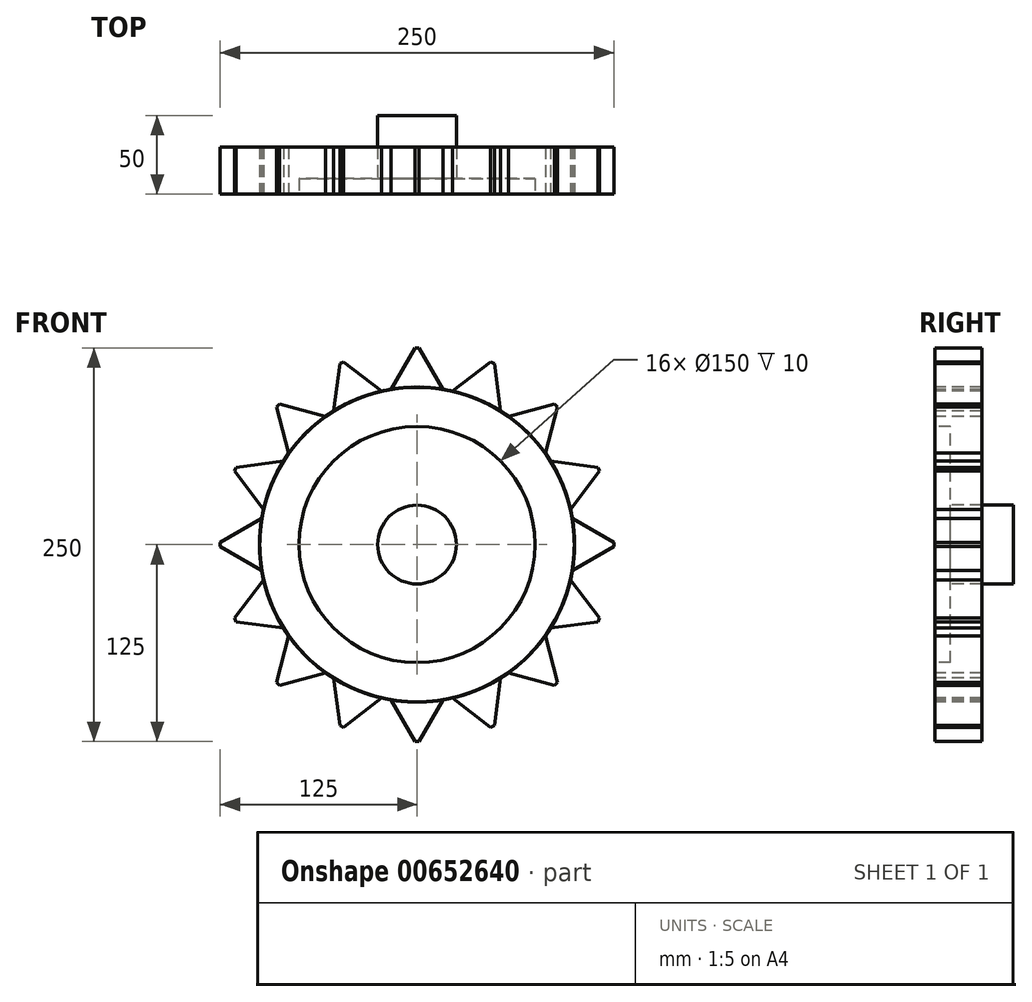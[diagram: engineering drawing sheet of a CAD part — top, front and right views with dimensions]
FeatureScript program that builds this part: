
annotation { "Feature Type Name" : "Feature", "Feature Type Description" : "" }
export const myFeature = defineFeature(function(context is Context, id is Id, definition is map)
    precondition{}
    {
        {
            var Q0;
            Q0=qCreatedBy(makeId("Front.planeOp"),FACE);
            var sketch = newSketch(context, id + "F0", { "sketchPlane" : qUnion([Q0])});
            skCircle(sketch, "E0", {"center": v(0, 0) * mm, "radius": 100 * mm});
            skSolve(sketch);
        }
        {
            var Q0;
            Q0=makeQuery(id+"F0.imprint","IMPRINT",FACE,{"disambiguationData":[TD([[makeQuery(id+"F0.imprint","IMPRINT",EDGE,{"derivedFrom":sQuery(id+"F0.wireOp",EDGE,"E0")}),1.0]])]});
            extrude(context, id + "F1", {"entities" : qUnion([Q0]), "oppositeDirection" : true, "depth" : 30 * mm, "offsetDistance" : 25 * mm});
        }
        {
            var Q0;
            Q0=makeQuery(id+"F1.opExtrude","CAP_FACE",FACE,{"disambiguationData":[OSD([sQuery(id+"F0.wireOp",EDGE,"E0")])],"isStart":true});
            var sketch = newSketch(context, id + "F2", { "sketchPlane" : qUnion([Q0])});
            skLineSegment(sketch, "E1", {"start": v(-23.1, 97.3) * mm, "end": v(-23.1, 87.3) * mm, "construction": true});
            skLineSegment(sketch, "E2", {"start": v(-23.1, 87.3) * mm, "end": v(23.1, 87.3) * mm, "construction": true});
            skLineSegment(sketch, "E3", {"start": v(23.1, 87.3) * mm, "end": v(23.1, 97.3) * mm, "construction": true});
            skLineSegment(sketch, "E4", {"start": v(23.1, 97.3) * mm, "end": v(23.1, 127.3) * mm, "construction": true});
            skLineSegment(sketch, "E5", {"start": v(23.1, 127.3) * mm, "end": v(-23.1, 127.3) * mm, "construction": true});
            skLineSegment(sketch, "E6", {"start": v(-23.1, 127.3) * mm, "end": v(-23.1, 97.3) * mm, "construction": true});
            skLineSegment(sketch, "E7", {"start": v(0, 127.3) * mm, "end": v(0, 87.3) * mm, "construction": true});
            skLineSegment(sketch, "E8", {"start": v(0, 127.3) * mm, "end": v(-23.1, 87.3) * mm, "construction": true});
            skLineSegment(sketch, "E9", {"start": v(23.1, 87.3) * mm, "end": v(0, 127.3) * mm, "construction": true});
            skLineSegment(sketch, "E10", {"start": v(0, 100) * mm, "end": v(0, 125) * mm, "construction": true});
            skLineSegment(sketch, "E11", {"start": v(0, 125) * mm, "end": v(1.33, 125) * mm, "construction": true});
            skLineSegment(sketch, "E12", {"start": v(1.33, 125) * mm, "end": v(0, 125) * mm, "construction": true});
            skLineSegment(sketch, "E13", {"start": v(0, 125) * mm, "end": v(-1.33, 125) * mm});
            skLineSegment(sketch, "E14", {"start": v(-1.33, 125) * mm, "end": v(-16.56, 98.62) * mm});
            skLineSegment(sketch, "E15", {"start": v(-16.56, 98.62) * mm, "end": v(-1.33, 125) * mm});
            skLineSegment(sketch, "E16", {"start": v(0, 125) * mm, "end": v(1.33, 125) * mm});
            skLineSegment(sketch, "E17", {"start": v(1.33, 125) * mm, "end": v(16.56, 98.62) * mm});
            skLineSegment(sketch, "E18", {"start": v(16.56, 98.62) * mm, "end": v(-16.56, 98.62) * mm});
            skSolve(sketch);
        }
        {
            var Q0;
            Q0=qSketchRegion(id+"F2",true);
            extrude(context, id + "F3", {"entities" : qUnion([Q0]), "operationType" : NewBodyOperationType.ADD, "oppositeDirection" : true, "depth" : 30 * mm, "offsetDistance" : 25 * mm});
        }
        {
            var Q0;
            Q0=qCreatedBy(makeId("Top.planeOp"),FACE);
            var sketch = newSketch(context, id + "F4", { "sketchPlane" : qUnion([Q0])});
            skLineSegment(sketch, "E19", {"start": v(0, 76.88) * mm, "end": v(0, -72) * mm, "construction": true});
            skSolve(sketch);
        }
        {
            var Q0;
            Q0=makeQuery(id+"F1.opExtrude","SWEPT_BODY",BODY,{"disambiguationData":[OSD([sQuery(id+"F0.wireOp",EDGE,"E0")])]});
            var Q1;
            Q1=sQuery(id+"F4.wireOp",EDGE,"E19");
            circularPattern(context, id + "F5", {"entities" : qUnion([Q0]), "axis" : qUnion([Q1]), "angle" : 360 * degree, "instanceCount" : 16, "equalSpace" : true});
        }
        {
            var Q0;
            Q0=makeQuery(id+"F3.boolean.opBoolean","MERGE",FACE,{"derivedFrom":[makeQuery(id+"F1.opExtrude","CAP_FACE",FACE,{"disambiguationData":[OSD([sQuery(id+"F0.wireOp",EDGE,"E0")])],"isStart":true}),makeQuery(id+"F3.opExtrude","CAP_FACE",FACE,{"disambiguationData":[OSD([sQuery(id+"F2.wireOp",EDGE,"E13"),sQuery(id+"F2.wireOp",EDGE,"E15"),sQuery(id+"F2.wireOp",EDGE,"E16"),sQuery(id+"F2.wireOp",EDGE,"E17"),sQuery(id+"F2.wireOp",EDGE,"E18")])],"isStart":true})]});
            var sketch = newSketch(context, id + "F6", { "sketchPlane" : qUnion([Q0])});
            skCircle(sketch, "E20", {"center": v(0, 0) * mm, "radius": 25 * mm});
            skSolve(sketch);
        }
        {
            var Q0;
            Q0=makeQuery(id+"F6.imprint","IMPRINT",FACE,{"disambiguationData":[TD([[makeQuery(id+"F6.imprint","IMPRINT",EDGE,{"derivedFrom":sQuery(id+"F6.wireOp",EDGE,"E20")}),1.0]])]});
            var Q1;
            Q1=sQuery(id+"F6.wireOp",EDGE,"E20");
            extrude(context, id + "F7", {"entities" : qUnion([Q0]), "surfaceEntities" : qUnion([Q1]), "oppositeDirection" : true, "depth" : 50 * mm, "offsetDistance" : 25 * mm});
        }
        {
            var Q0;
            Q0=makeQuery(id+"F3.boolean.opBoolean","MERGE",FACE,{"derivedFrom":[makeQuery(id+"F1.opExtrude","CAP_FACE",FACE,{"disambiguationData":[OSD([sQuery(id+"F0.wireOp",EDGE,"E0")])],"isStart":true}),makeQuery(id+"F3.opExtrude","CAP_FACE",FACE,{"disambiguationData":[OSD([sQuery(id+"F2.wireOp",EDGE,"E13"),sQuery(id+"F2.wireOp",EDGE,"E15"),sQuery(id+"F2.wireOp",EDGE,"E16"),sQuery(id+"F2.wireOp",EDGE,"E17"),sQuery(id+"F2.wireOp",EDGE,"E18")])],"isStart":true})]});
            var sketch = newSketch(context, id + "F8", { "sketchPlane" : qUnion([Q0])});
            skCircle(sketch, "E21", {"center": v(0, 0) * mm, "radius": 75 * mm});
            skSolve(sketch);
        }
        {
            var Q0;
            Q0=makeQuery(id+"F8.imprint","IMPRINT",FACE,{"disambiguationData":[TD([[makeQuery(id+"F8.imprint","IMPRINT",EDGE,{"derivedFrom":sQuery(id+"F8.wireOp",EDGE,"E21")}),1.0]])]});
            extrude(context, id + "F9", {"entities" : qUnion([Q0]), "operationType" : NewBodyOperationType.REMOVE, "oppositeDirection" : true, "depth" : 10 * mm, "offsetDistance" : 25 * mm});
        }
        {
            var Q0;
            {var subQ0=sQuery(id+"F8.wireOp",EDGE,"E21");Q0=makeQuery(id+"F9.boolean.opBoolean","COPY",FACE,{"disambiguationData":[TD([makeQuery(id+"F9.opExtrude","SWEPT_FACE",FACE,{"disambiguationData":[OSD([subQ0])]})]),OD(1.0)],"derivedFrom":makeQuery(id+"F9.opExtrude","CAP_FACE",FACE,{"disambiguationData":[OSD([subQ0])],"isStart":false})});}
            var sketch = newSketch(context, id + "F10", { "sketchPlane" : qUnion([Q0])});
            skCircle(sketch, "E22", {"center": v(0, 45) * mm, "radius": 12.5 * mm});
            skSolve(sketch);
        }
        {
            var Q0;
            Q0=sQuery(id+"F10.wireOp",VERTEX,"E22.center");
            var Q1;
            Q1=makeQuery(id+"F7.opExtrude","SWEPT_BODY",BODY,{"disambiguationData":[OSD([sQuery(id+"F6.wireOp",EDGE,"E20")])]});
            hole(context, id + "F11", {"style" : HoleStyle.SIMPLE, "endStyle" : HoleEndStyle.THROUGH, "holeDiameter" : 25 * mm, "majorDiameter" : 5 * mm, "isTappedThrough" : true, "tappedDepth" : 12 * mm, "tapClearance" : 3, "locations" : qUnion([Q0]), "scope" : qUnion([Q1])});
        }
    });
